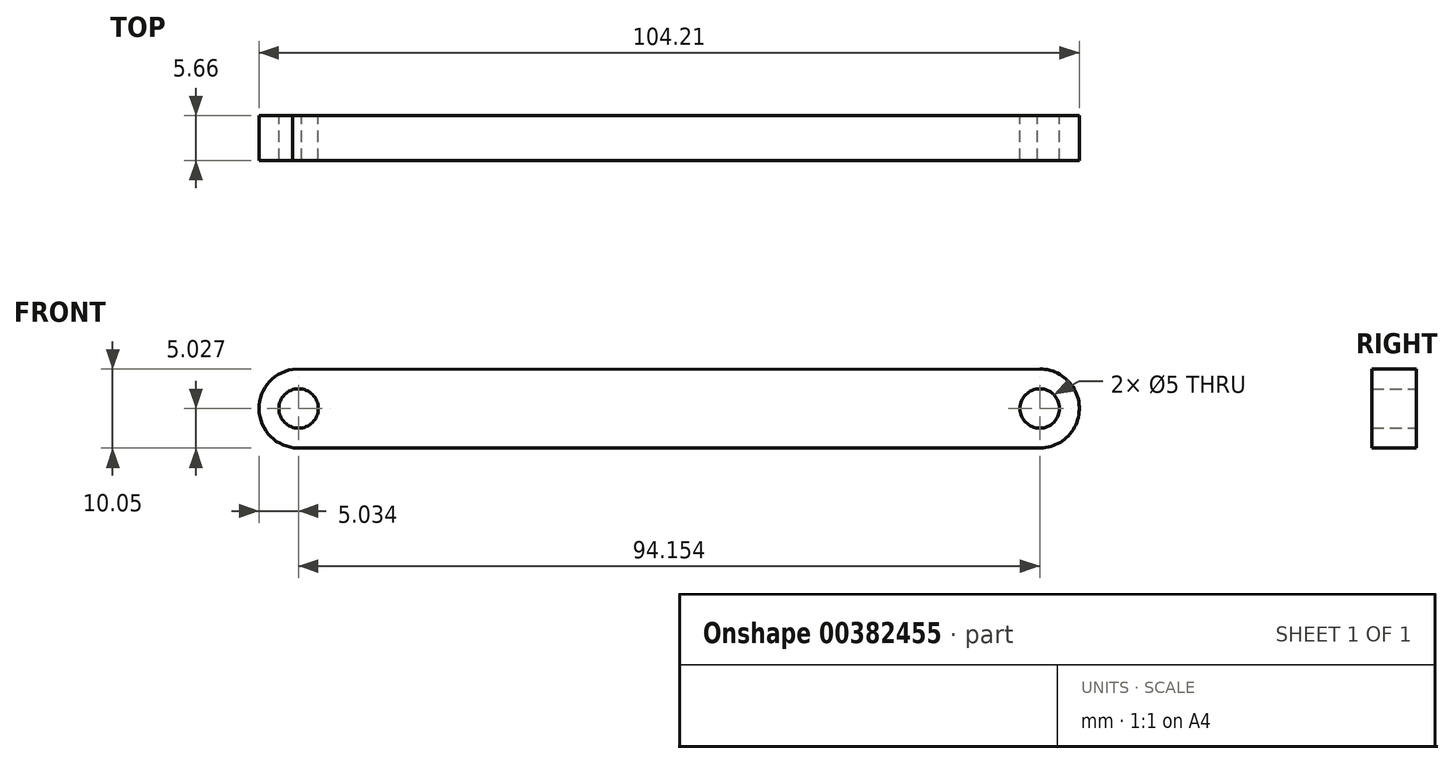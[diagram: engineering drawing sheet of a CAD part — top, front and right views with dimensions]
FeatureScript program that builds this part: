
annotation { "Feature Type Name" : "Feature", "Feature Type Description" : "" }
export const myFeature = defineFeature(function(context is Context, id is Id, definition is map)
    precondition{}
    {
        {
            var Q0;
            Q0=qCreatedBy(makeId("Front.planeOp"),FACE);
            var sketch = newSketch(context, id + "F0", { "sketchPlane" : qUnion([Q0])});
            skLineSegment(sketch, "E0", {"start": v(-37.38, 13.14) * mm, "end": v(56.66, 13.14) * mm});
            skArc(sketch, "E1", {"start": v(-38.53, 23.13) * mm, "mid": v(-42.76, 17.58) * mm, "end": v(-37.38, 13.14) * mm});
            skArc(sketch, "E2", {"start": v(56.12, 13.14) * mm, "mid": v(61.4, 18.02) * mm, "end": v(56.39, 23.18) * mm});
            skLineSegment(sketch, "E3", {"start": v(-38.53, 23.13) * mm, "end": v(56.39, 23.18) * mm});
            skCircle(sketch, "E4", {"center": v(-37.77, 18.16) * mm, "radius": 2.5 * mm});
            skCircle(sketch, "E5", {"center": v(56.39, 18.16) * mm, "radius": 2.5 * mm});
            skSolve(sketch);
        }
        {
            var Q0;
            Q0 = qSketchRegion(id + "F0", true);
            extrude(context, id + "F1", {"entities" : qUnion([Q0]), "depth" : 5.66 * mm});
        }
    });
